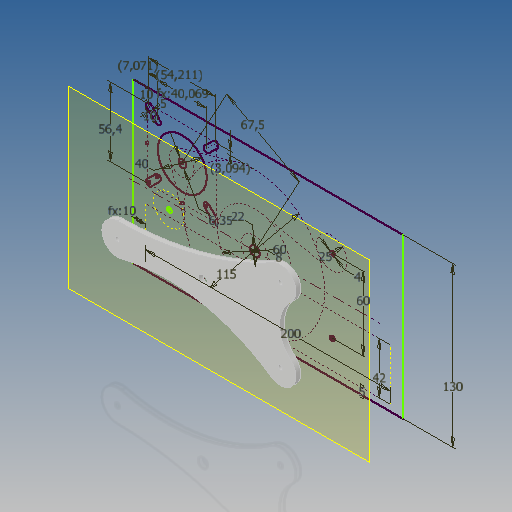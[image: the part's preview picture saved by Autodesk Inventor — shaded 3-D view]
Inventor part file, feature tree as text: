
AUTODESK INVENTOR PART (.ipt)
format: ipt  version: 2017 (Build 210142000, 142)  size: 166,912 bytes
history: native  units: mm
features: other x5, sketch x2, plane x1, extrude x1, reference x1
ambient origin geometry x8: Origin, YZ Plane, XZ Plane, XY Plane, X Axis, Y Axis, Z Axis, Center Point
bodies: Body1 (feature_tree)
feature tree (10):
  other  "Sólido1"
  sketch  "Boceto1"  dims[d0=6.35mm d1=56.4mm]
  plane  "Plano de trabajo1"
  extrude  "Extrusión1"  Depth=56.4mm
  sketch  "Boceto2"  dims[d2=67.5mm d3=40.0mm d4=200.0mm d5=42.0mm d6=8.0mm d7=3.094466mm d8=5.0mm d9=40.068932mm d10=10.0mm d11=54.211068mm d12=7.071068mm d13=4.0mm d14=115.0mm d15=25.0mm d16=60.0mm d17=60.0mm d18=5.0mm d19=10.0mm d20=22.0mm d21=130.0mm d22=10.0mm d23=38.0mm d24=4.0mm d25=0.0mm]
  reference  "Referencia1"
  other  "<userpath>\Dropbox\E\Caja Motriz\transmision Engranajes.iam"
  other  "transmision Engranajes.iam"
  other  "Plato Carrete:1"
  other  "carrete:1"
